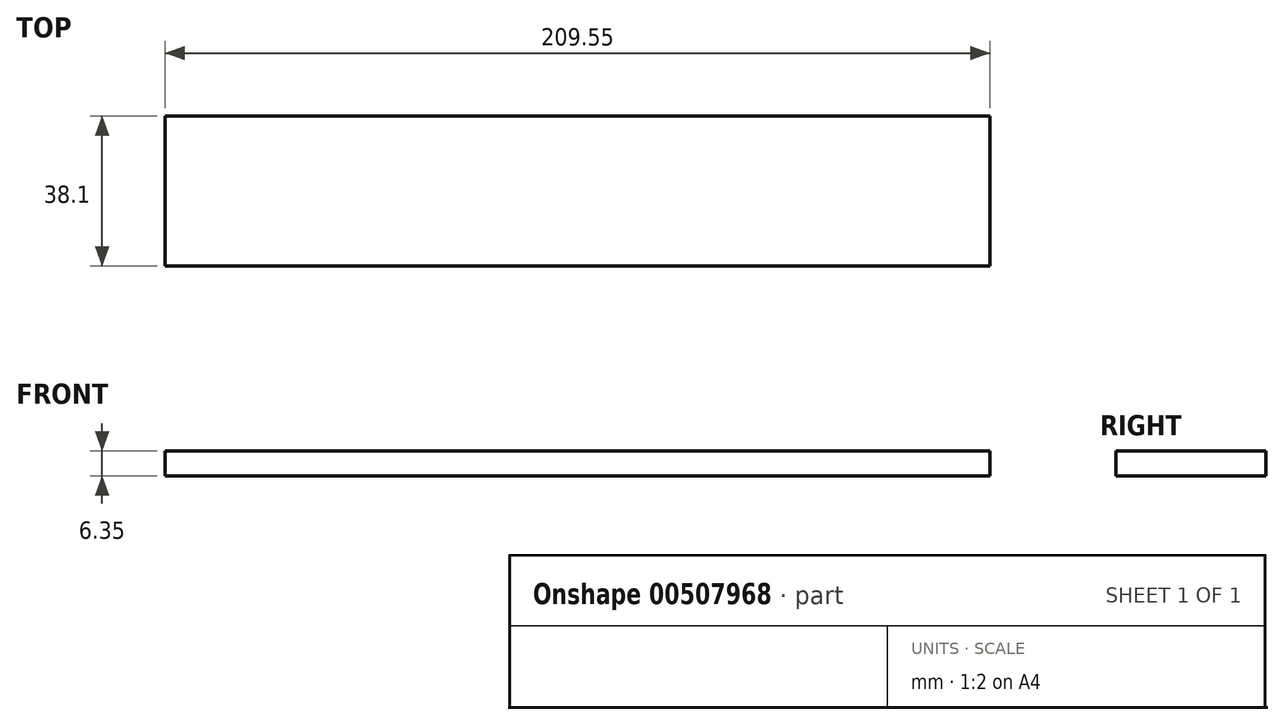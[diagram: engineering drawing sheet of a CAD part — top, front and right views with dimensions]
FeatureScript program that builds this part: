
annotation { "Feature Type Name" : "Feature", "Feature Type Description" : "" }
export const myFeature = defineFeature(function(context is Context, id is Id, definition is map)
    precondition{}
    {
        {
            var Q0;
            Q0=qCreatedBy(makeId("Top.planeOp"),FACE);
            var sketch = newSketch(context, id + "F0", { "sketchPlane" : qUnion([Q0])});
            skLineSegment(sketch, "E0.bottom", {"start": v(0, 0) * mm, "end": v(209.55, 0) * mm});
            skLineSegment(sketch, "E0.top", {"start": v(0, -38.1) * mm, "end": v(209.55, -38.1) * mm});
            skLineSegment(sketch, "E0.left", {"start": v(0, 0) * mm, "end": v(0, -38.1) * mm});
            skLineSegment(sketch, "E0.right", {"start": v(209.55, 0) * mm, "end": v(209.55, -38.1) * mm});
            skSolve(sketch);
        }
        {
            var Q0;
            Q0=makeQuery(id+"F0.imprint","IMPRINT",FACE,{"disambiguationData":[TD([[makeQuery(id+"F0.imprint","IMPRINT",EDGE,{"derivedFrom":sQuery(id+"F0.wireOp",EDGE,"E0.bottom")}),-1.0]])]});
            extrude(context, id + "F1", {"entities" : qUnion([Q0]), "depth" : 6.35 * mm, "offsetDistance" : 25.4 * mm});
        }
    });
